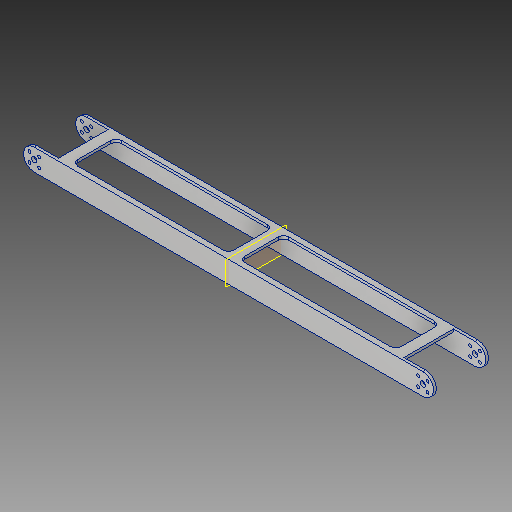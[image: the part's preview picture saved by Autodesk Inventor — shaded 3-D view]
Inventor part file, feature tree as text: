
AUTODESK INVENTOR PART (.ipt)
format: ipt  version: 2019 (Build 230136000, 136)  size: 240,128 bytes
history: native  units: in
note: dims shown in document units (in); Inventor stores cm internally (conversion verified against a paired STEP export)
features: sketch x5, extrude x4, fillet x3, projected_geometry x3, hole x1, plane x1, mirror x1
ambient origin geometry x8: Origin, YZ Plane, XZ Plane, XY Plane, X Axis, Y Axis, Z Axis, Center Point
bodies: Solid1 (feature_tree)
feature tree (18):
  extrude  "Extrusion1"  Depth=2.2935in
  extrude  "Extrusion2"  Depth=0.125in
  extrude  "Extrusion3"  Depth=2.5435in
  hole  "Hole1"  [1 undecoded]
  fillet  "Fillet1"  Radius=0.25in
  extrude  "Extrusion4"  Depth=1.0in
  fillet  "Fillet2"  Radius=0.5in
  plane  "Work Plane1"
  mirror  "Mirror1"
  fillet  "Fillet3"  Radius=0.25in
  sketch  "Sketch1"  dims[d0=1.0in d2=2.2935in]
  sketch  "Sketch3"  dims[d3=0.875in d4=0.125in]
  projected_geometry  "Projected Loop2"
  sketch  "Sketch4"  dims[d5=19.0in d6=0.0in d14=2.5435in]
  projected_geometry  "Projected Loop3"
  sketch  "Sketch5"  dims[d16=1.5in d17=0.125in d18=0.0in d19=0.25in]
  sketch  "Sketch6"  dims[d20=0.5in d21=1.0in d22=0.5in d23=0.25in d24=0.5in d25=5.0in d26=0.0in d27=1.5in d28=2.2935in d29=0.125in d30=2.2935in d31=0.125in d32=0.125in d33=0.445in d34=0.445in d35=0.2775in d36=0.2775in d37=0.445in d38=0.445in d39=0.2775in d40=0.2775in d43=1.0003in d47=0.445in d48=0.445in d49=0.2777in d50=0.2777in d51=0.445in d52=0.445in d53=0.2777in d55=0.1378in d56=0.75in d57=0.375in d58=0.25in d59=0.5635in d60=5.0in d61=0.8108in d62=0.5in d63=0.7227in d65=16.0in d66=2.5435in d67=0.25in d68=2.0435in d69=0.5in d70=7.25in d71=1.0in d72=0.0in d73=0.25in d74=0.25in]
  projected_geometry  "Projected Loop4"
note: 1 required parameter value undecoded (feature->parameter linkage not recoverable at this tier; creation-order binding heuristic only, values carry confidence <= 0.55)
